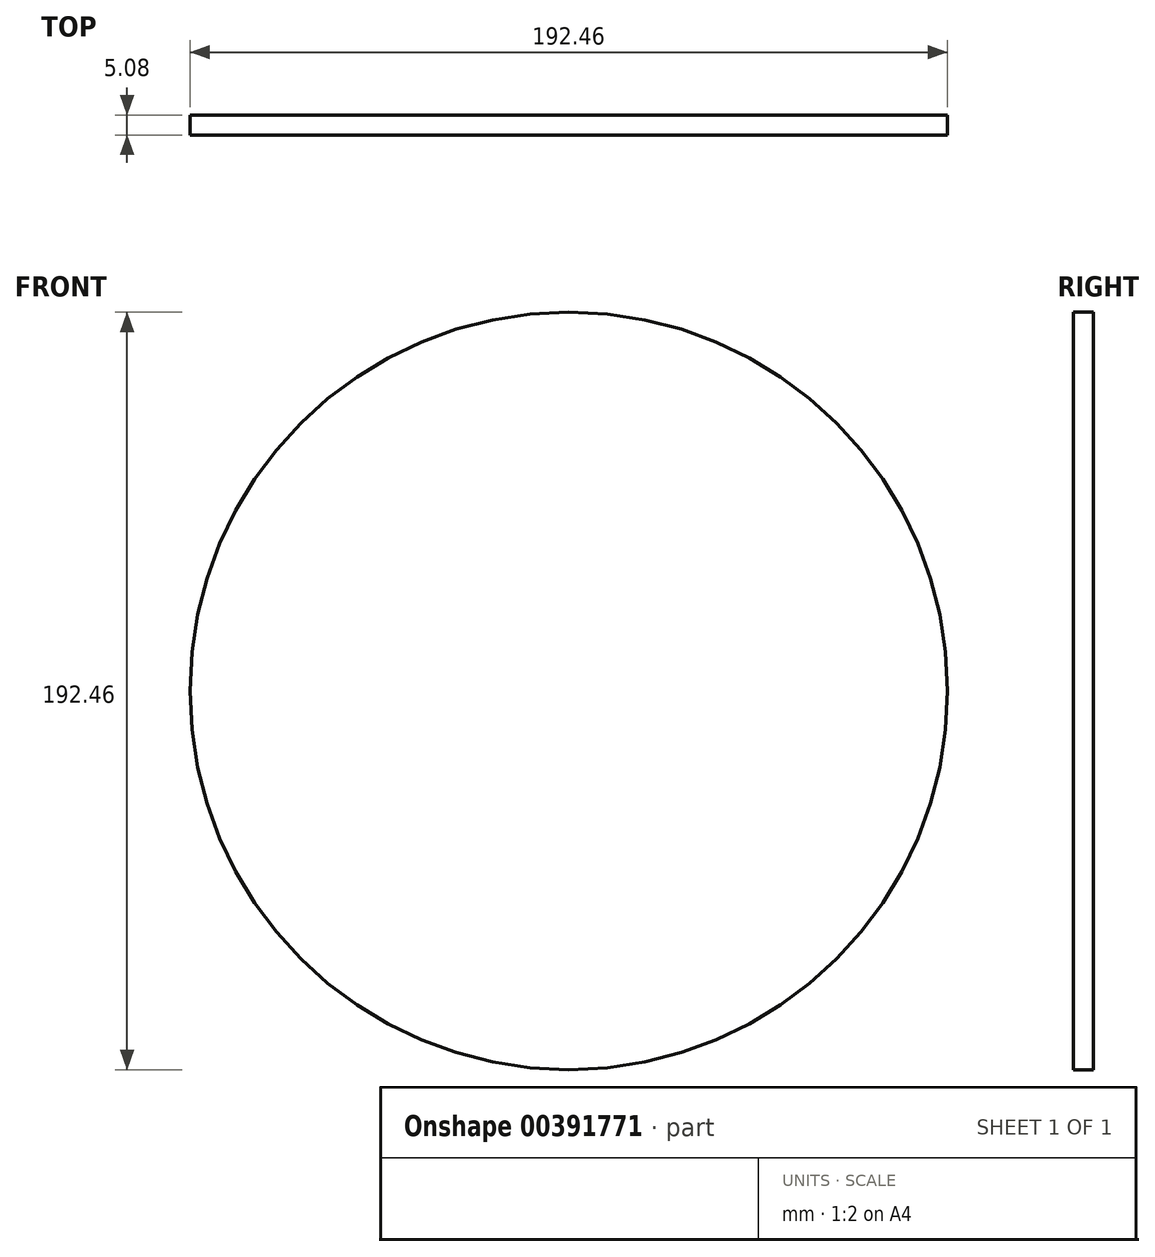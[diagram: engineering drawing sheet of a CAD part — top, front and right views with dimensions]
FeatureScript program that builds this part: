
annotation { "Feature Type Name" : "Feature", "Feature Type Description" : "" }
export const myFeature = defineFeature(function(context is Context, id is Id, definition is map)
    precondition{}
    {
        {
            var Q0;
            Q0=qCreatedBy(makeId("Front.planeOp"),FACE);
            var sketch = newSketch(context, id + "F0", { "sketchPlane" : qUnion([Q0])});
            skLineSegment(sketch, "E0.bottom", {"start": v(-184.1, -101.63) * mm, "end": v(184.57, -101.63) * mm});
            skLineSegment(sketch, "E0.top", {"start": v(-184.1, 103.03) * mm, "end": v(184.57, 103.03) * mm});
            skLineSegment(sketch, "E0.left", {"start": v(-184.1, -101.63) * mm, "end": v(-184.1, 103.03) * mm});
            skLineSegment(sketch, "E0.right", {"start": v(184.57, -101.63) * mm, "end": v(184.57, 103.03) * mm});
            skSolve(sketch);
        }
        {
            var Q0;
            Q0 = qSketchRegion(id + "F0", true);
            extrude(context, id + "F1", {"entities" : qUnion([Q0]), "depth" : 12.7 * mm});
        }
        {
            var Q0;
            Q0=makeQuery(id+"F1.opExtrude","CAP_FACE",FACE,{"disambiguationData":[OSD([sQuery(id+"F0.wireOp",EDGE,"E0.bottom"),sQuery(id+"F0.wireOp",EDGE,"E0.top"),sQuery(id+"F0.wireOp",EDGE,"E0.left"),sQuery(id+"F0.wireOp",EDGE,"E0.right")])],"isStart":false});
            var sketch = newSketch(context, id + "F2", { "sketchPlane" : qUnion([Q0])});
            skCircle(sketch, "E1", {"center": v(0, 0) * mm, "radius": 96.23 * mm});
            skSolve(sketch);
        }
        {
            var Q0;
            Q0=makeQuery(id+"F2.imprint","IMPRINT",FACE,{"disambiguationData":[TD([[makeQuery(id+"F2.imprint","IMPRINT",EDGE,{"derivedFrom":sQuery(id+"F2.wireOp",EDGE,"E1")}),-1.0]])]});
            extrude(context, id + "F3", {"entities" : qUnion([Q0]), "operationType" : NewBodyOperationType.REMOVE, "oppositeDirection" : true, "depth" : 12.7 * mm});
        }
        {
            var Q0;
            Q0=makeQuery(id+"F2.imprint","IMPRINT",FACE,{"disambiguationData":[TD([[makeQuery(id+"F2.imprint","IMPRINT",EDGE,{"derivedFrom":sQuery(id+"F2.wireOp",EDGE,"E1")}),1.0]])]});
            var Q1;
            Q1=makeQuery(id+"F0.imprint","IMPRINT",FACE,{"disambiguationData":[TD([[makeQuery(id+"F0.imprint","IMPRINT",EDGE,{"derivedFrom":sQuery(id+"F0.wireOp",EDGE,"E0.bottom")}),1.0]])]});
            extrude(context, id + "F4", {"entities" : qUnion([Q0, Q1]), "operationType" : NewBodyOperationType.REMOVE, "oppositeDirection" : true, "depth" : 7.62 * mm});
        }
    });
